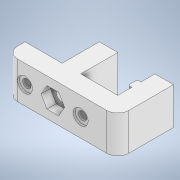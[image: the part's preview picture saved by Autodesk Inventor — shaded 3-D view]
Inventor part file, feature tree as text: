
AUTODESK INVENTOR PART (.ipt)
format: ipt  version: 2020 (Build 240168000, 168)  size: 195,072 bytes
history: native  units: mm
features: extrude x4, sketch x2, other x1, fillet x1
ambient origin geometry x8: Origin, YZ Plane, XZ Plane, XY Plane, X Axis, Y Axis, Z Axis, Center Point
bodies: Body1 (feature_tree)
feature tree (8):
  other  "Bryła1"
  extrude  "Wyciągnięcie proste1"  Depth=20.0mm
  sketch  "Szkic2"
  extrude  "Wyciągnięcie proste2"  Depth=20.0mm
  extrude  "Wyciągnięcie proste3"  Depth=20.0mm
  fillet  "Zaokrąglenie1"  Radius=20.0mm
  extrude  "Wyciągnięcie proste4"  Depth=50.0mm
  sketch  "Szkic1"
